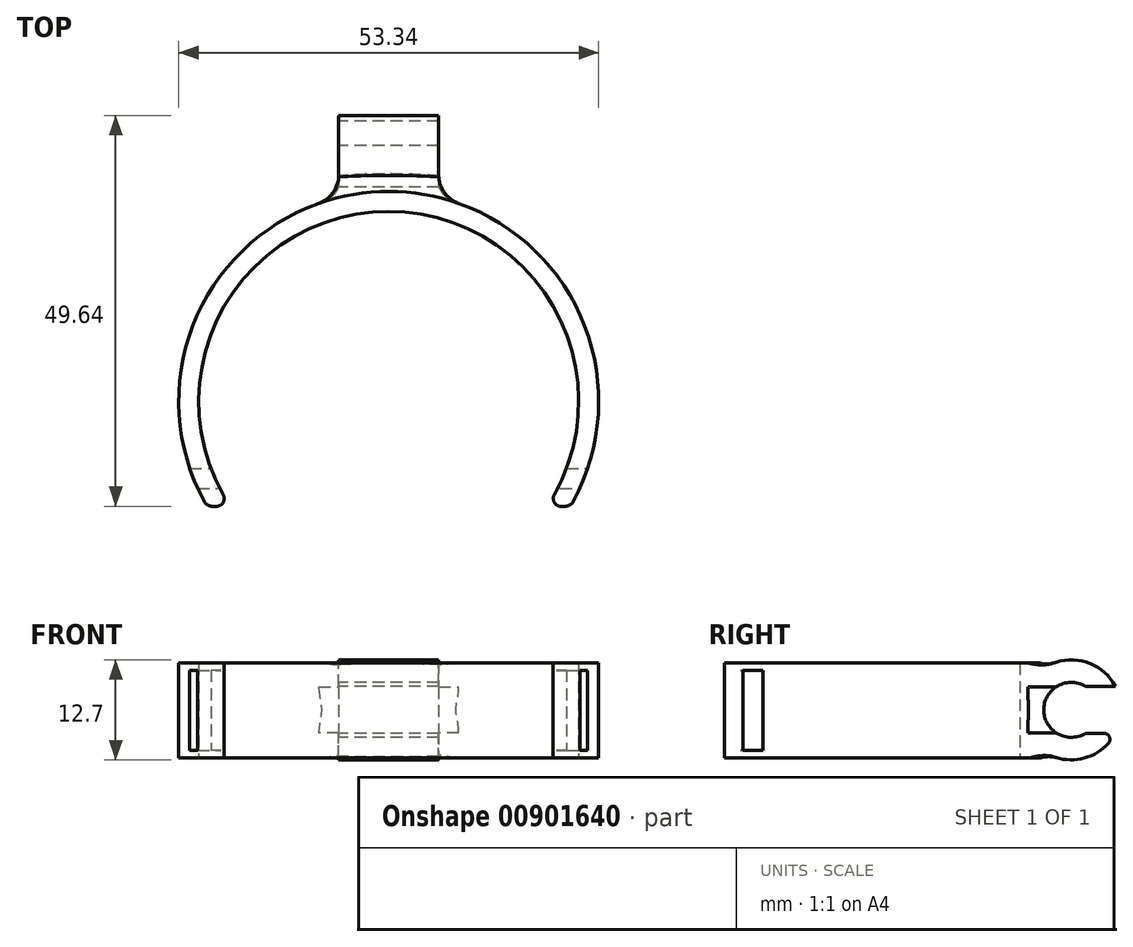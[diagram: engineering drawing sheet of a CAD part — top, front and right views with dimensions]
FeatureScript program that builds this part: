
annotation { "Feature Type Name" : "Feature", "Feature Type Description" : "" }
export const myFeature = defineFeature(function(context is Context, id is Id, definition is map)
    precondition{}
    {
        {
            var Q0;
            Q0=qCreatedBy(makeId("Top.planeOp"),FACE);
            var sketch = newSketch(context, id + "F0", { "sketchPlane" : qUnion([Q0])});
            skCircle(sketch, "E0", {"center": v(0, 0) * mm, "radius": 26.67 * mm});
            skSolve(sketch);
        }
        {
            var Q0;
            Q0=qCreatedBy(makeId("Top.planeOp"),FACE);
            var sketch = newSketch(context, id + "F1", { "sketchPlane" : qUnion([Q0])});
            skCircle(sketch, "E1", {"center": v(0, 0) * mm, "radius": 24.13 * mm});
            skSolve(sketch);
        }
        {
            var Q0;
            Q0=makeQuery(id+"F0.imprint","IMPRINT",FACE,{"disambiguationData":[TD([[makeQuery(id+"F0.imprint","IMPRINT",EDGE,{"derivedFrom":sQuery(id+"F0.wireOp",EDGE,"E0")}),1.0]])]});
            extrude(context, id + "F2", {"entities" : qUnion([Q0]), "depth" : 12.06 * mm, "offsetDistance" : 25.4 * mm});
        }
        {
            var Q0;
            Q0=makeQuery(id+"F1.imprint","IMPRINT",FACE,{"disambiguationData":[TD([[makeQuery(id+"F1.imprint","IMPRINT",EDGE,{"derivedFrom":sQuery(id+"F1.wireOp",EDGE,"E1")}),1.0]])]});
            extrude(context, id + "F3", {"entities" : qUnion([Q0]), "operationType" : NewBodyOperationType.REMOVE, "depth" : 25.4 * mm, "offsetDistance" : 25.4 * mm});
        }
        {
            var Q0;
            Q0=qCreatedBy(makeId("Right.planeOp"),FACE);
            var sketch = newSketch(context, id + "F4", { "sketchPlane" : qUnion([Q0])});
            skCircle(sketch, "E2", {"center": v(30.68, 6.12) * mm, "radius": 6.35 * mm});
            skCircle(sketch, "E3", {"center": v(30.68, 6.12) * mm, "radius": 3.5 * mm});
            skSolve(sketch);
        }
        {
            var Q0;
            Q0=makeQuery(id+"F4.imprint","IMPRINT",FACE,{"disambiguationData":[TD([[makeQuery(id+"F4.imprint","IMPRINT",EDGE,{"derivedFrom":sQuery(id+"F4.wireOp",EDGE,"E2")}),1.0]])]});
            extrude(context, id + "F5", {"entities" : qUnion([Q0]), "operationType" : NewBodyOperationType.ADD, "endBound" : BoundingType.SYMMETRIC, "depth" : 12.7 * mm, "offsetDistance" : 25.4 * mm});
        }
        {
            var Q0;
            Q0=makeQuery(id+"F5.boolean.opBoolean","INTERSECT",EDGE,{"disambiguationData":[OD(1.0)],"derivedFrom":[makeQuery(id+"F2.opExtrude","SWEPT_FACE",FACE,{"disambiguationData":[OSD([sQuery(id+"F0.wireOp",EDGE,"E0")])]}),makeQuery(id+"F5.opExtrude","SWEPT_FACE",FACE,{"disambiguationData":[OSD([sQuery(id+"F4.wireOp",EDGE,"E2")])]})]});
            var Q1;
            Q1=makeQuery(id+"F5.boolean.opBoolean","INTERSECT",EDGE,{"derivedFrom":[makeQuery(id+"F2.opExtrude","SWEPT_FACE",FACE,{"disambiguationData":[OSD([sQuery(id+"F0.wireOp",EDGE,"E0")])]}),makeQuery(id+"F5.opExtrude","CAP_FACE",FACE,{"disambiguationData":[OSD([sQuery(id+"F4.wireOp",EDGE,"E2"),sQuery(id+"F4.wireOp",EDGE,"E3")])],"isStart":false})]});
            var Q2;
            Q2=makeQuery(id+"F5.boolean.opBoolean","INTERSECT",EDGE,{"disambiguationData":[OD(0.0)],"derivedFrom":[makeQuery(id+"F2.opExtrude","SWEPT_FACE",FACE,{"disambiguationData":[OSD([sQuery(id+"F0.wireOp",EDGE,"E0")])]}),makeQuery(id+"F5.opExtrude","SWEPT_FACE",FACE,{"disambiguationData":[OSD([sQuery(id+"F4.wireOp",EDGE,"E2")])]})]});
            var Q3;
            Q3=makeQuery(id+"F5.boolean.opBoolean","INTERSECT",EDGE,{"derivedFrom":[makeQuery(id+"F2.opExtrude","SWEPT_FACE",FACE,{"disambiguationData":[OSD([sQuery(id+"F0.wireOp",EDGE,"E0")])]}),makeQuery(id+"F5.opExtrude","CAP_FACE",FACE,{"disambiguationData":[OSD([sQuery(id+"F4.wireOp",EDGE,"E2"),sQuery(id+"F4.wireOp",EDGE,"E3")])],"isStart":true})]});
            fillet(context, id + "F6", {"entities" : qUnion([Q0, Q1, Q2, Q3]), "radius" : 3.8 * mm, "tangentPropagation" : true, "allowEdgeOverflow" : false});
        }
        {
            var Q0;
            Q0=makeQuery(id+"F2.opExtrude","CAP_FACE",FACE,{"disambiguationData":[OSD([sQuery(id+"F0.wireOp",EDGE,"E0")])],"isStart":false});
            var sketch = newSketch(context, id + "F7", { "sketchPlane" : qUnion([Q0])});
            skLineSegment(sketch, "E4.bottom", {"start": v(-28.45, -13.35) * mm, "end": v(27.86, -13.35) * mm});
            skLineSegment(sketch, "E4.top", {"start": v(-28.45, -28.03) * mm, "end": v(27.86, -28.03) * mm});
            skLineSegment(sketch, "E4.left", {"start": v(-28.45, -13.35) * mm, "end": v(-28.45, -28.03) * mm});
            skLineSegment(sketch, "E4.right", {"start": v(27.86, -13.35) * mm, "end": v(27.86, -28.03) * mm});
            skSolve(sketch);
        }
        {
            var Q0;
            Q0 = qSketchRegion(id + "F7", true);
            extrude(context, id + "F8", {"entities" : qUnion([Q0]), "operationType" : NewBodyOperationType.REMOVE, "oppositeDirection" : true, "depth" : 25.4 * mm, "offsetDistance" : 25.4 * mm});
        }
        {
            var Q0;
            Q0=makeQuery(id+"F8.boolean.opBoolean","INTERSECT",EDGE,{"disambiguationData":[OD(0.0)],"derivedFrom":[makeQuery(id+"F3.boolean.opBoolean","COPY",FACE,{"derivedFrom":makeQuery(id+"F3.opExtrude","SWEPT_FACE",FACE,{"disambiguationData":[OSD([sQuery(id+"F1.wireOp",EDGE,"E1")])]})}),makeQuery(id+"F8.opExtrude","SWEPT_FACE",FACE,{"disambiguationData":[OSD([sQuery(id+"F7.wireOp",EDGE,"E4.bottom")])]})]});
            var Q1;
            Q1=makeQuery(id+"F8.boolean.opBoolean","INTERSECT",EDGE,{"disambiguationData":[OD(1.0)],"derivedFrom":[makeQuery(id+"F3.boolean.opBoolean","COPY",FACE,{"derivedFrom":makeQuery(id+"F3.opExtrude","SWEPT_FACE",FACE,{"disambiguationData":[OSD([sQuery(id+"F1.wireOp",EDGE,"E1")])]})}),makeQuery(id+"F8.opExtrude","SWEPT_FACE",FACE,{"disambiguationData":[OSD([sQuery(id+"F7.wireOp",EDGE,"E4.bottom")])]})]});
            fillet(context, id + "F9", {"entities" : qUnion([Q0, Q1]), "radius" : 1.02 * mm, "tangentPropagation" : true, "allowEdgeOverflow" : false});
        }
        {
            var Q0;
            Q0=makeQuery(id+"F8.boolean.opBoolean","INTERSECT",EDGE,{"disambiguationData":[OD(1.0)],"derivedFrom":[makeQuery(id+"F2.opExtrude","SWEPT_FACE",FACE,{"disambiguationData":[OSD([sQuery(id+"F0.wireOp",EDGE,"E0")])]}),makeQuery(id+"F8.opExtrude","SWEPT_FACE",FACE,{"disambiguationData":[OSD([sQuery(id+"F7.wireOp",EDGE,"E4.bottom")])]})]});
            var Q1;
            Q1=makeQuery(id+"F8.boolean.opBoolean","INTERSECT",EDGE,{"disambiguationData":[OD(0.0)],"derivedFrom":[makeQuery(id+"F2.opExtrude","SWEPT_FACE",FACE,{"disambiguationData":[OSD([sQuery(id+"F0.wireOp",EDGE,"E0")])]}),makeQuery(id+"F8.opExtrude","SWEPT_FACE",FACE,{"disambiguationData":[OSD([sQuery(id+"F7.wireOp",EDGE,"E4.bottom")])]})]});
            fillet(context, id + "F10", {"entities" : qUnion([Q0, Q1]), "radius" : 1.27 * mm, "tangentPropagation" : true, "allowEdgeOverflow" : false});
        }
        {
            var Q0;
            Q0=makeQuery(id+"F5.opExtrude","CAP_FACE",FACE,{"disambiguationData":[OSD([sQuery(id+"F4.wireOp",EDGE,"E2"),sQuery(id+"F4.wireOp",EDGE,"E3")])],"isStart":true});
            var sketch = newSketch(context, id + "F11", { "sketchPlane" : qUnion([Q0])});
            skLineSegment(sketch, "E5.bottom", {"start": v(-30.26, 9.1) * mm, "end": v(-38.1, 9.1) * mm});
            skLineSegment(sketch, "E5.top", {"start": v(-30.26, 3.14) * mm, "end": v(-38.1, 3.14) * mm});
            skLineSegment(sketch, "E5.left", {"start": v(-30.26, 9.1) * mm, "end": v(-30.26, 3.14) * mm});
            skLineSegment(sketch, "E5.right", {"start": v(-38.1, 9.1) * mm, "end": v(-38.1, 3.14) * mm});
            skPoint(sketch, "E5.middle", {"position": v(-34.18, 6.12) * mm});
            skSolve(sketch);
        }
        {
            var Q0;
            {var subQ0=sQuery(id+"F11.wireOp",EDGE,"E5.bottom");var subQ1=makeQuery(id+"F5.opExtrude","CAP_EDGE",EDGE,{"disambiguationData":[OSD([sQuery(id+"F4.wireOp",EDGE,"E3")])],"isStart":true});var subQ2=makeQuery(id+"F11.imprint","INTERSECT",VERTEX,{"derivedFrom":[subQ1,subQ0]});Q0=makeQuery(id+"F11.imprint","IMPRINT",FACE,{"disambiguationData":[TD([[makeQuery(id+"F11.imprint","IMPRINT",EDGE,{"disambiguationData":[TD([[subQ2,-1.0]])],"derivedFrom":subQ0}),1.0]])]});}
            extrude(context, id + "F12", {"entities" : qUnion([Q0]), "operationType" : NewBodyOperationType.REMOVE, "oppositeDirection" : true, "depth" : 25.4 * mm, "offsetDistance" : 25.4 * mm});
        }
        {
            var Q0;
            Q0=makeQuery(id+"F12.boolean.opBoolean","COPY",EDGE,{"derivedFrom":makeQuery(id+"F12.opExtrude","SWEPT_EDGE",EDGE,{"disambiguationData":[OSD([sQuery(id+"F4.wireOp",EDGE,"E2"),sQuery(id+"F11.wireOp",EDGE,"E5.bottom")])]})});
            var Q1;
            Q1=makeQuery(id+"F12.boolean.opBoolean","COPY",EDGE,{"derivedFrom":makeQuery(id+"F12.opExtrude","SWEPT_EDGE",EDGE,{"disambiguationData":[OSD([sQuery(id+"F4.wireOp",EDGE,"E2"),sQuery(id+"F11.wireOp",EDGE,"E5.top")])]})});
            fillet(context, id + "F13", {"entities" : qUnion([Q0, Q1]), "radius" : 0.76 * mm, "tangentPropagation" : true, "allowEdgeOverflow" : false});
        }
        {
            var Q0;
            Q0=qCreatedBy(makeId("Right.planeOp"),FACE);
            var sketch = newSketch(context, id + "F14", { "sketchPlane" : qUnion([Q0])});
            skLineSegment(sketch, "E6.bottom", {"start": v(-11.05, 11.15) * mm, "end": v(-8.5, 11.15) * mm});
            skLineSegment(sketch, "E6.top", {"start": v(-11.05, 0.99) * mm, "end": v(-8.5, 0.99) * mm});
            skLineSegment(sketch, "E6.left", {"start": v(-11.05, 11.15) * mm, "end": v(-11.05, 0.99) * mm});
            skLineSegment(sketch, "E6.right", {"start": v(-8.5, 11.15) * mm, "end": v(-8.5, 0.99) * mm});
            skPoint(sketch, "E6.middle", {"position": v(-9.78, 6.07) * mm});
            skSolve(sketch);
        }
        {
            var Q0;
            Q0=makeQuery(id+"F14.imprint","IMPRINT",FACE,{"disambiguationData":[TD([[makeQuery(id+"F14.imprint","IMPRINT",EDGE,{"derivedFrom":sQuery(id+"F14.wireOp",EDGE,"E6.bottom")}),-1.0]])]});
            extrude(context, id + "F15", {"entities" : qUnion([Q0]), "operationType" : NewBodyOperationType.REMOVE, "endBound" : BoundingType.SYMMETRIC, "oppositeDirection" : true, "depth" : 76.2 * mm, "offsetDistance" : 25.4 * mm});
        }
        {
            var Q0;
            Q0=makeQuery(id+"F15.boolean.opBoolean","INTERSECT",EDGE,{"disambiguationData":[OD(0.0)],"derivedFrom":[makeQuery(id+"F3.boolean.opBoolean","COPY",FACE,{"derivedFrom":makeQuery(id+"F3.opExtrude","SWEPT_FACE",FACE,{"disambiguationData":[OSD([sQuery(id+"F1.wireOp",EDGE,"E1")])]})}),makeQuery(id+"F15.opExtrude","SWEPT_FACE",FACE,{"disambiguationData":[OSD([sQuery(id+"F14.wireOp",EDGE,"E6.left")])]})]});
            var Q1;
            Q1=makeQuery(id+"F15.boolean.opBoolean","INTERSECT",EDGE,{"disambiguationData":[OD(1.0)],"derivedFrom":[makeQuery(id+"F3.boolean.opBoolean","COPY",FACE,{"derivedFrom":makeQuery(id+"F3.opExtrude","SWEPT_FACE",FACE,{"disambiguationData":[OSD([sQuery(id+"F1.wireOp",EDGE,"E1")])]})}),makeQuery(id+"F15.opExtrude","SWEPT_FACE",FACE,{"disambiguationData":[OSD([sQuery(id+"F14.wireOp",EDGE,"E6.left")])]})]});
            fillet(context, id + "F16", {"entities" : qUnion([Q0, Q1]), "radius" : 0.5 * mm, "tangentPropagation" : true, "allowEdgeOverflow" : false});
        }
    });
